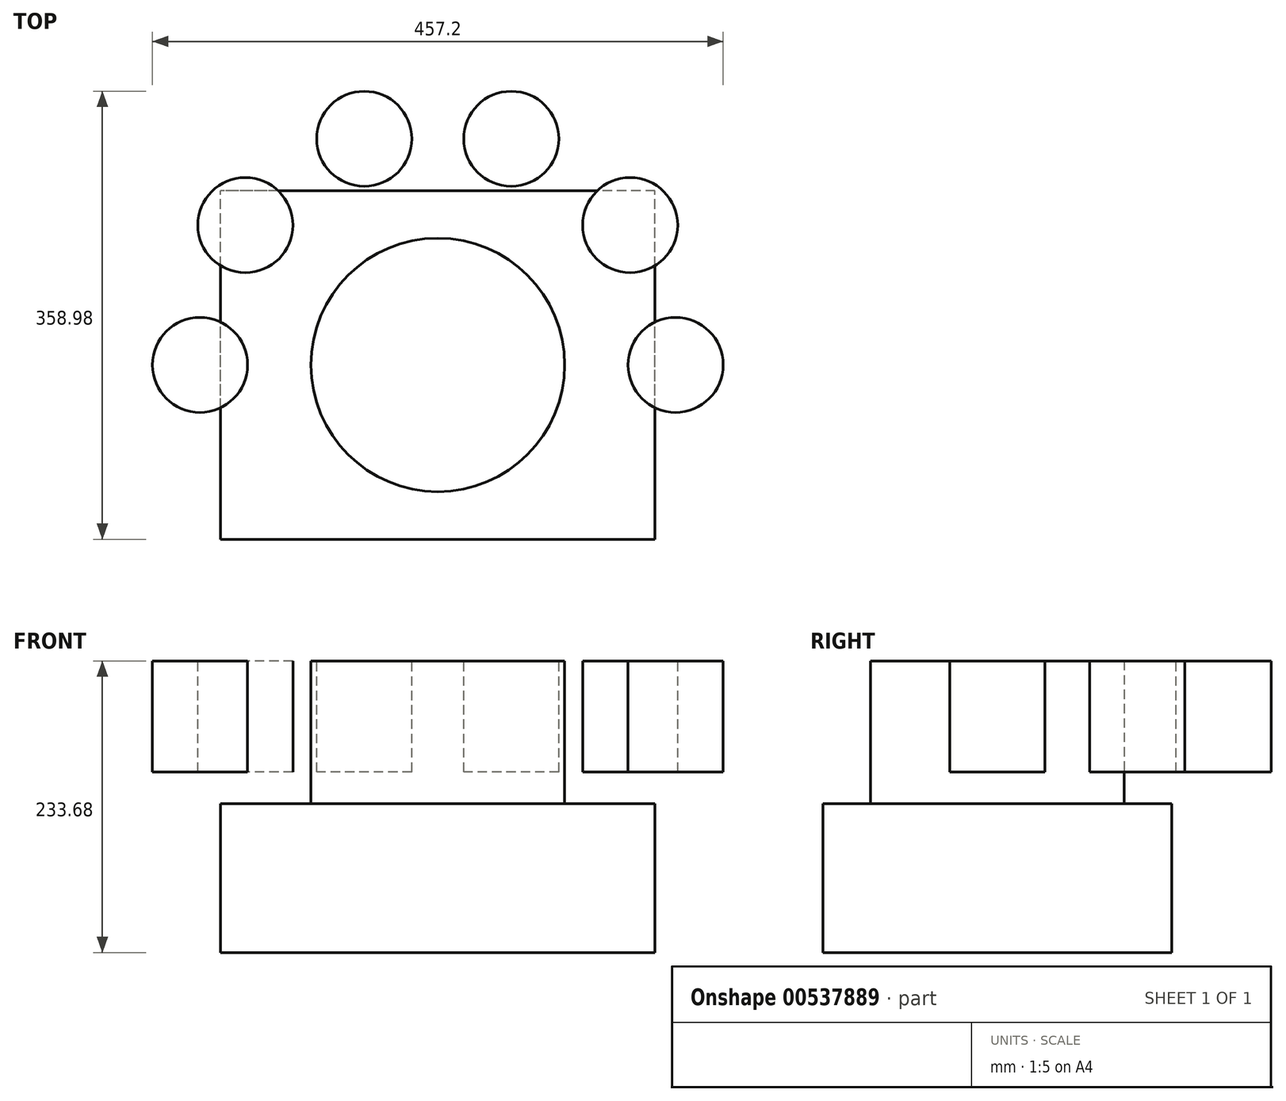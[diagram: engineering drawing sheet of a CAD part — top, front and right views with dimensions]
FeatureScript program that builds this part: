
annotation { "Feature Type Name" : "Feature", "Feature Type Description" : "" }
export const myFeature = defineFeature(function(context is Context, id is Id, definition is map)
    precondition{}
    {
        {
            var Q0;
            Q0=qCreatedBy(makeId("Top.planeOp"),FACE);
            var sketch = newSketch(context, id + "F0", { "sketchPlane" : qUnion([Q0])});
            skLineSegment(sketch, "E0.bottom", {"start": v(174, -139.7) * mm, "end": v(-174, -139.7) * mm});
            skLineSegment(sketch, "E0.top", {"start": v(174, 139.7) * mm, "end": v(-174, 139.7) * mm});
            skLineSegment(sketch, "E0.left", {"start": v(174, -139.7) * mm, "end": v(174, 139.7) * mm});
            skLineSegment(sketch, "E0.right", {"start": v(-174, -139.7) * mm, "end": v(-174, 139.7) * mm});
            skPoint(sketch, "E0.middle", {"position": v(0, 0) * mm});
            skSolve(sketch);
        }
        {
            var Q0;
            Q0 = qSketchRegion(id + "F0", true);
            extrude(context, id + "F1", {"entities" : qUnion([Q0]), "depth" : 119.38 * mm, "offsetDistance" : 25.4 * mm});
        }
        {
            var Q0;
            Q0=makeQuery(id+"F1.opExtrude","CAP_FACE",FACE,{"disambiguationData":[OSD([sQuery(id+"F0.wireOp",EDGE,"E0.bottom"),sQuery(id+"F0.wireOp",EDGE,"E0.top"),sQuery(id+"F0.wireOp",EDGE,"E0.left"),sQuery(id+"F0.wireOp",EDGE,"E0.right")])],"isStart":false});
            var sketch = newSketch(context, id + "F2", { "sketchPlane" : qUnion([Q0])});
            skCircle(sketch, "E1", {"center": v(0, 0) * mm, "radius": 101.6 * mm});
            skSolve(sketch);
        }
        {
            var Q0;
            Q0 = qSketchRegion(id + "F2", true);
            extrude(context, id + "F3", {"entities" : qUnion([Q0]), "operationType" : NewBodyOperationType.ADD, "depth" : 114.3 * mm, "offsetDistance" : 25.4 * mm});
        }
        {
            var Q0;
            Q0=makeQuery(id+"F3.opExtrude","CAP_FACE",FACE,{"disambiguationData":[OSD([sQuery(id+"F2.wireOp",EDGE,"E1")])],"isStart":false});
            var sketch = newSketch(context, id + "F4", { "sketchPlane" : qUnion([Q0])});
            skCircle(sketch, "E2", {"center": v(0, 0) * mm, "radius": 152.4 * mm, "construction": true});
            skCircle(sketch, "E3", {"center": v(-190.5, 0) * mm, "radius": 38.1 * mm});
            skLineSegment(sketch, "E4", {"start": v(0, 0) * mm, "end": v(-190.5, 0) * mm, "construction": true});
            skCircle(sketch, "E5.1.0", {"center": v(-154.12, 111.97) * mm, "radius": 38.1 * mm});
            skLineSegment(sketch, "E5.1.1", {"start": v(0, 0) * mm, "end": v(-154.12, 111.97) * mm, "construction": true});
            skCircle(sketch, "E5.2.0", {"center": v(-58.87, 181.18) * mm, "radius": 38.1 * mm});
            skLineSegment(sketch, "E5.2.1", {"start": v(0, 0) * mm, "end": v(-58.87, 181.18) * mm, "construction": true});
            skCircle(sketch, "E5.3.0", {"center": v(58.87, 181.18) * mm, "radius": 38.1 * mm});
            skLineSegment(sketch, "E5.3.1", {"start": v(0, 0) * mm, "end": v(58.87, 181.18) * mm, "construction": true});
            skCircle(sketch, "E5.4.0", {"center": v(154.12, 111.97) * mm, "radius": 38.1 * mm});
            skLineSegment(sketch, "E5.4.1", {"start": v(0, 0) * mm, "end": v(154.12, 111.97) * mm, "construction": true});
            skCircle(sketch, "E5.5.0", {"center": v(190.5, 0) * mm, "radius": 38.1 * mm});
            skLineSegment(sketch, "E5.5.1", {"start": v(0, 0) * mm, "end": v(190.5, 0) * mm, "construction": true});
            skLineSegment(sketch, "E5.anchor2", {"start": v(0, 0) * mm, "end": v(190.5, 0) * mm, "construction": true});
            skSolve(sketch);
        }
        {
            var Q0;
            Q0 = qSketchRegion(id + "F4", true);
            extrude(context, id + "F5", {"entities" : qUnion([Q0]), "oppositeDirection" : true, "depth" : 88.9 * mm, "offsetDistance" : 25.4 * mm});
        }
    });
